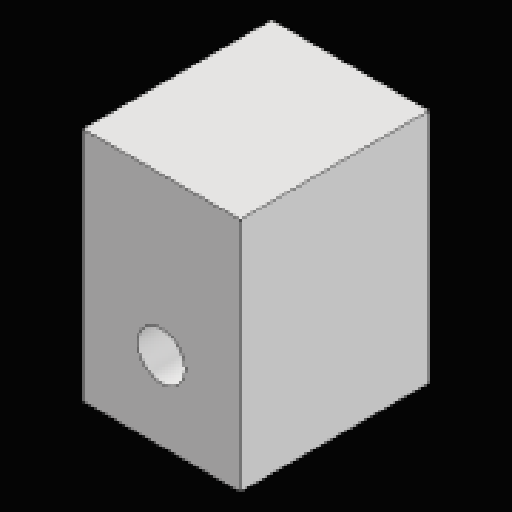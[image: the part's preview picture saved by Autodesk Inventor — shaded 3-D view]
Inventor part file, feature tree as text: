
AUTODESK INVENTOR PART (.ipt)
format: ipt  version: 2023.2 (Build 272271030, 271C)  size: 98,304 bytes
history: native  units: mm
features: extrude x2, sketch x2, projected_geometry x1
ambient origin geometry x8: Origin, YZ Plane, XZ Plane, XY Plane, X Axis, Y Axis, Z Axis, Center Point
bodies: Solid1 (feature_tree)
feature tree (5):
  extrude  "Extrusion1"  Depth=10.0mm
  extrude  "Extrusion2"  Depth=3.0mm
  sketch  "Sketch1"  dims[d0=10.0mm d1=10.0mm]
  sketch  "Sketch2"  dims[d2=12.0mm d3=0.0mm d4=3.0mm d6=0.0mm d7=0.0mm d8=5.0mm d9=7.0mm]
  projected_geometry  "Projected Loop1"
